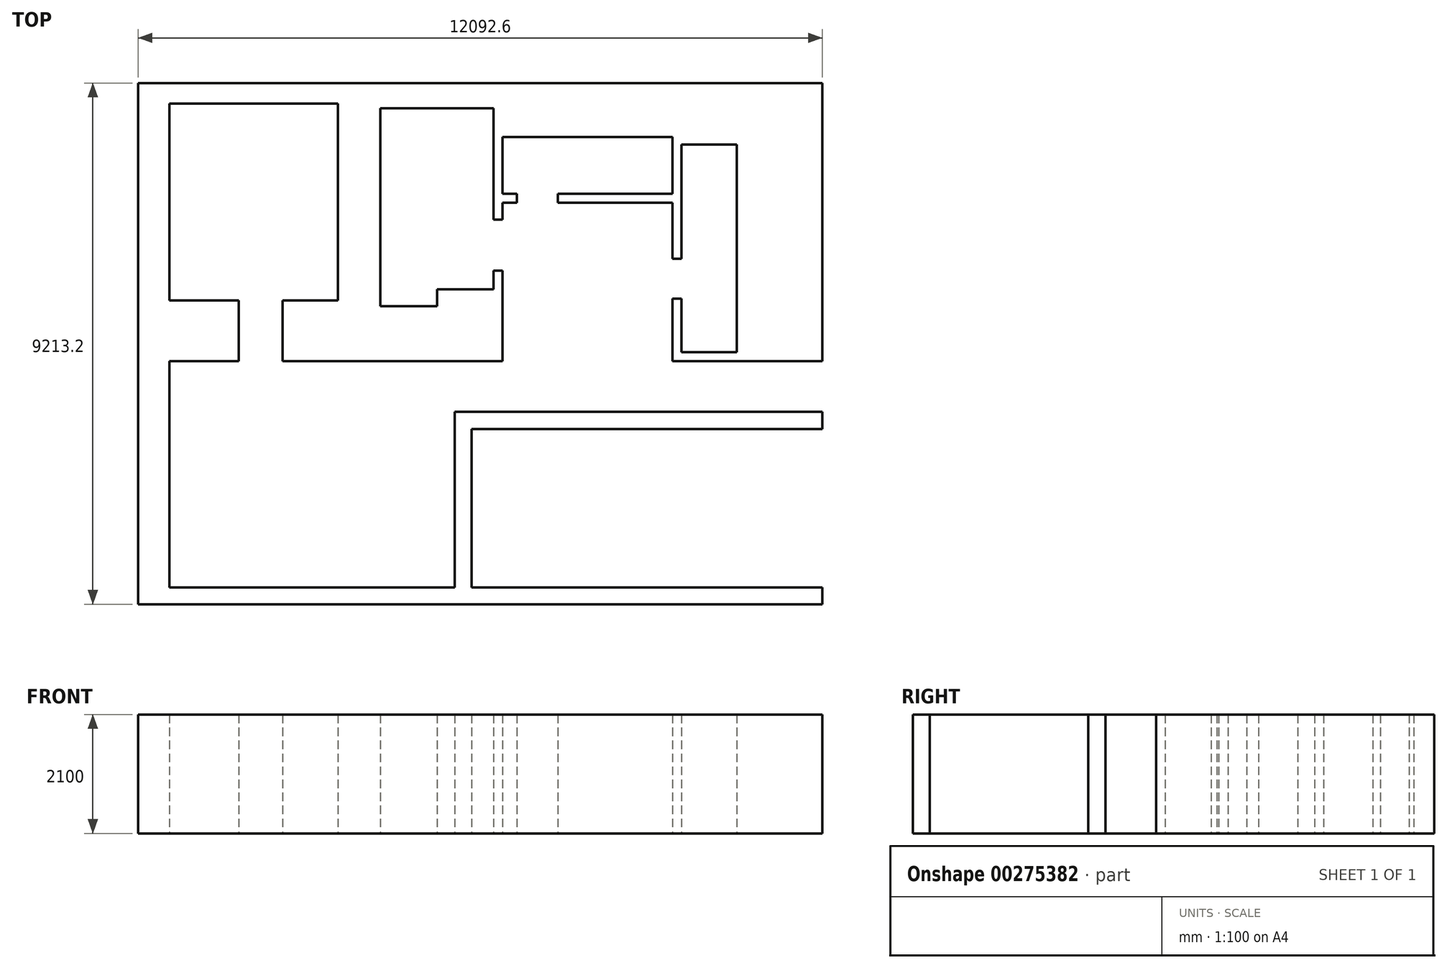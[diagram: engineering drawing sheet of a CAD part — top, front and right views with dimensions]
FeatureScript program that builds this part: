
annotation { "Feature Type Name" : "Feature", "Feature Type Description" : "" }
export const myFeature = defineFeature(function(context is Context, id is Id, definition is map)
    precondition{}
    {
        {
            var Q0;
            Q0=qCreatedBy(makeId("Top.planeOp"),FACE);
            var sketch = newSketch(context, id + "F0", { "sketchPlane" : qUnion([Q0])});
            skLineSegment(sketch, "E0", {"start": v(0, 0) * mm, "end": v(0, -9213.2) * mm});
            skLineSegment(sketch, "E1", {"start": v(0, -9213.2) * mm, "end": v(12092.6, -9213.2) * mm});
            skLineSegment(sketch, "E2", {"start": v(12092.6, -9213.2) * mm, "end": v(12092.6, -8913.2) * mm});
            skLineSegment(sketch, "E3", {"start": v(12092.6, 0) * mm, "end": v(0, 0) * mm});
            skLineSegment(sketch, "E4", {"start": v(12092.6, -6113.2) * mm, "end": v(5892.6, -6113.2) * mm});
            skLineSegment(sketch, "E5", {"start": v(12092.6, -5813.2) * mm, "end": v(5592.6, -5813.2) * mm});
            skLineSegment(sketch, "E6", {"start": v(5592.6, -5813.2) * mm, "end": v(5592.6, -8913.2) * mm});
            skLineSegment(sketch, "E7", {"start": v(5592.6, -8913.2) * mm, "end": v(551.5, -8913.2) * mm});
            skLineSegment(sketch, "E8", {"start": v(551.5, -8913.2) * mm, "end": v(551.5, -4918.2) * mm});
            skLineSegment(sketch, "E9", {"start": v(551.5, -4918.2) * mm, "end": v(1781, -4918.2) * mm});
            skLineSegment(sketch, "E10", {"start": v(1781, -4918.2) * mm, "end": v(1781, -3843.56) * mm});
            skLineSegment(sketch, "E11", {"start": v(1781, -3843.56) * mm, "end": v(551.5, -3843.56) * mm});
            skLineSegment(sketch, "E12", {"start": v(551.5, -3843.56) * mm, "end": v(551.5, -363.02) * mm});
            skLineSegment(sketch, "E13", {"start": v(551.5, -363.02) * mm, "end": v(3528.75, -363.02) * mm});
            skLineSegment(sketch, "E14", {"start": v(3528.75, -363.02) * mm, "end": v(3528.75, -3843.56) * mm});
            skLineSegment(sketch, "E15", {"start": v(3528.75, -3843.56) * mm, "end": v(2552.65, -3843.56) * mm});
            skLineSegment(sketch, "E16", {"start": v(2552.65, -3843.56) * mm, "end": v(2552.65, -4918.2) * mm});
            skLineSegment(sketch, "E17", {"start": v(2552.65, -4918.2) * mm, "end": v(6442.6, -4918.2) * mm});
            skLineSegment(sketch, "E18", {"start": v(6442.6, -4918.2) * mm, "end": v(6442.6, -3313.2) * mm});
            skLineSegment(sketch, "E19", {"start": v(6442.6, -3313.2) * mm, "end": v(6282.6, -3313.2) * mm});
            skLineSegment(sketch, "E20", {"start": v(6282.6, -3313.2) * mm, "end": v(6282.6, -3644.36) * mm});
            skLineSegment(sketch, "E21", {"start": v(5282.6, -3944.36) * mm, "end": v(4282.6, -3944.36) * mm});
            skLineSegment(sketch, "E22", {"start": v(4282.6, -3944.36) * mm, "end": v(4282.6, -444.36) * mm});
            skLineSegment(sketch, "E23", {"start": v(4282.6, -444.36) * mm, "end": v(6282.6, -444.36) * mm});
            skLineSegment(sketch, "E24", {"start": v(6282.6, -444.36) * mm, "end": v(6282.6, -2413.2) * mm});
            skLineSegment(sketch, "E25", {"start": v(6282.6, -2413.2) * mm, "end": v(6442.6, -2413.2) * mm});
            skLineSegment(sketch, "E26", {"start": v(6442.6, -2413.2) * mm, "end": v(6442.6, -2113.2) * mm});
            skLineSegment(sketch, "E27", {"start": v(6442.6, -2113.2) * mm, "end": v(6692.6, -2113.2) * mm});
            skLineSegment(sketch, "E28", {"start": v(5892.6, -6113.2) * mm, "end": v(5892.6, -8913.2) * mm});
            skLineSegment(sketch, "E29", {"start": v(5892.6, -8913.2) * mm, "end": v(12092.6, -8913.2) * mm});
            skLineSegment(sketch, "E30.trimOffspring", {"start": v(12092.6, -6113.2) * mm, "end": v(12092.6, -5813.2) * mm});
            skLineSegment(sketch, "E31", {"start": v(12092.6, -4918.2) * mm, "end": v(9442.6, -4918.2) * mm});
            skLineSegment(sketch, "E32", {"start": v(9442.6, -4918.2) * mm, "end": v(9442.6, -3808.2) * mm});
            skLineSegment(sketch, "E33.trimOffspring", {"start": v(12092.6, -4918.2) * mm, "end": v(12092.6, 0) * mm});
            skLineSegment(sketch, "E34", {"start": v(9442.6, -3808.2) * mm, "end": v(9602.6, -3808.2) * mm});
            skLineSegment(sketch, "E35", {"start": v(9602.6, -3808.2) * mm, "end": v(9602.6, -4758.2) * mm});
            skLineSegment(sketch, "E36", {"start": v(9602.6, -4758.2) * mm, "end": v(10582.6, -4758.2) * mm});
            skLineSegment(sketch, "E37", {"start": v(10582.6, -4758.2) * mm, "end": v(10582.6, -1088.2) * mm});
            skLineSegment(sketch, "E38", {"start": v(10582.6, -1088.2) * mm, "end": v(9602.6, -1088.2) * mm});
            skLineSegment(sketch, "E39", {"start": v(9602.6, -1088.2) * mm, "end": v(9602.6, -3108.2) * mm});
            skLineSegment(sketch, "E40", {"start": v(9602.6, -3108.2) * mm, "end": v(9442.6, -3108.2) * mm});
            skLineSegment(sketch, "E41", {"start": v(9442.6, -3108.2) * mm, "end": v(9442.6, -2113.2) * mm});
            skLineSegment(sketch, "E42", {"start": v(9442.6, -2113.2) * mm, "end": v(7420.6, -2113.2) * mm});
            skLineSegment(sketch, "E43", {"start": v(7420.6, -2113.2) * mm, "end": v(7420.6, -1953.2) * mm});
            skLineSegment(sketch, "E44", {"start": v(7420.6, -1953.2) * mm, "end": v(9442.6, -1953.2) * mm});
            skLineSegment(sketch, "E45", {"start": v(9442.6, -1953.2) * mm, "end": v(9442.6, -953.2) * mm});
            skLineSegment(sketch, "E46", {"start": v(9442.6, -953.2) * mm, "end": v(6442.6, -953.2) * mm});
            skLineSegment(sketch, "E47", {"start": v(6442.6, -953.2) * mm, "end": v(6442.6, -1953.2) * mm});
            skLineSegment(sketch, "E48", {"start": v(6442.6, -1953.2) * mm, "end": v(6692.6, -1953.2) * mm});
            skLineSegment(sketch, "E49", {"start": v(6692.6, -1953.2) * mm, "end": v(6692.6, -2113.2) * mm});
            skLineSegment(sketch, "E50", {"start": v(6282.6, -3644.36) * mm, "end": v(5282.6, -3644.36) * mm});
            skLineSegment(sketch, "E51", {"start": v(5282.6, -3644.36) * mm, "end": v(5282.6, -3944.36) * mm});
            skSolve(sketch);
        }
        {
            var Q0;
            Q0 = qSketchRegion(id + "F0", true);
            extrude(context, id + "F1", {"entities" : qUnion([Q0]), "depth" : 2100 * mm, "offsetDistance" : 25 * mm});
        }
    });
